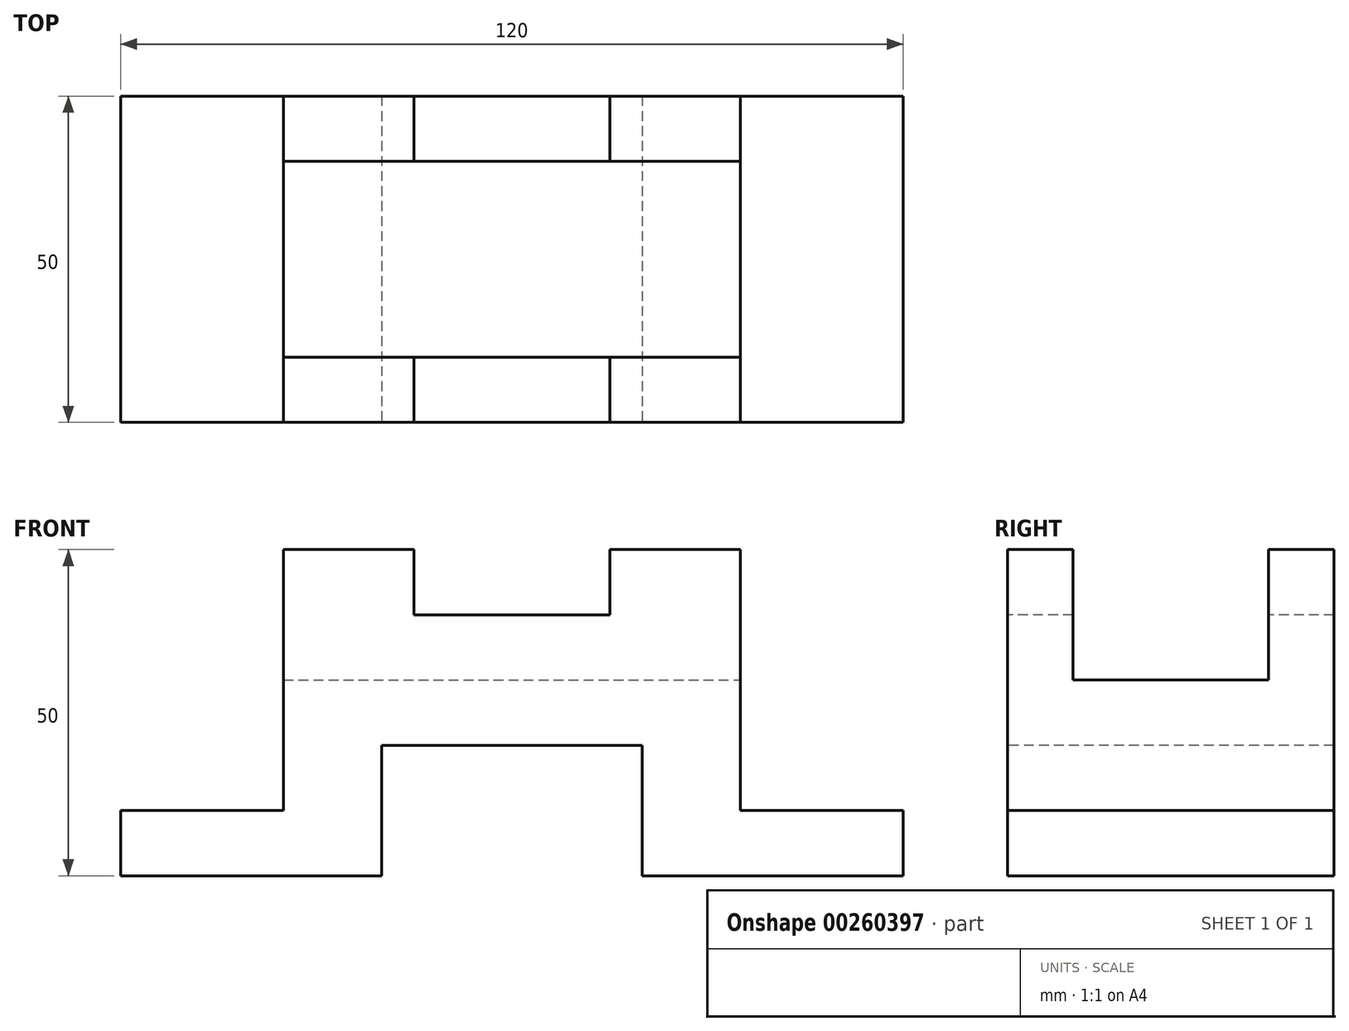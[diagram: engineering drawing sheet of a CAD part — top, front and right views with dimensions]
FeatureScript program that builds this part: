
annotation { "Feature Type Name" : "Feature", "Feature Type Description" : "" }
export const myFeature = defineFeature(function(context is Context, id is Id, definition is map)
    precondition{}
    {
        {
            assignVariable(context, id + "F0", {"name" : "B", "anyValue" : 50});
        }
        {
            var Q0;
            Q0=qCreatedBy(makeId("Top.planeOp"),FACE);
            var sketch = newSketch(context, id + "F1", { "sketchPlane" : qUnion([Q0])});
            skLineSegment(sketch, "E0.bottom", {"start": v(60, 25) * mm, "end": v(-60, 25) * mm});
            skLineSegment(sketch, "E0.top", {"start": v(60, -25) * mm, "end": v(-60, -25) * mm});
            skLineSegment(sketch, "E0.left", {"start": v(60, 25) * mm, "end": v(60, -25) * mm});
            skLineSegment(sketch, "E0.right", {"start": v(-60, 25) * mm, "end": v(-60, -25) * mm});
            skPoint(sketch, "E0.middle", {"position": v(0, 0) * mm});
            skSolve(sketch);
        }
        {
            var Q0;
            Q0 = qSketchRegion(id + "F1", true);
            extrude(context, id + "F2", {"entities" : qUnion([Q0]), "depth" : (getVariable(context, 'B')) * mm});
        }
        {
            var Q0;
            Q0=makeQuery(id+"F2.opExtrude","SWEPT_FACE",FACE,{"disambiguationData":[OSD([sQuery(id+"F1.wireOp",EDGE,"E0.top")])]});
            var sketch = newSketch(context, id + "F3", { "sketchPlane" : qUnion([Q0])});
            skLineSegment(sketch, "E1.bottom", {"start": v(-20, 20) * mm, "end": v(20, 20) * mm});
            skLineSegment(sketch, "E1.top", {"start": v(-20, -20) * mm, "end": v(20, -20) * mm});
            skLineSegment(sketch, "E1.left", {"start": v(-20, 20) * mm, "end": v(-20, -20) * mm});
            skLineSegment(sketch, "E1.right", {"start": v(20, 20) * mm, "end": v(20, -20) * mm});
            skPoint(sketch, "E1.middle", {"position": v(0, 0) * mm});
            skLineSegment(sketch, "E2.bottom", {"start": v(15, 40) * mm, "end": v(-15, 40) * mm});
            skLineSegment(sketch, "E2.top", {"start": v(15, 60) * mm, "end": v(-15, 60) * mm});
            skLineSegment(sketch, "E2.left", {"start": v(15, 40) * mm, "end": v(15, 60) * mm});
            skLineSegment(sketch, "E2.right", {"start": v(-15, 40) * mm, "end": v(-15, 60) * mm});
            skPoint(sketch, "E2.middle", {"position": v(0, 50) * mm});
            skLineSegment(sketch, "E3.bottom", {"start": v(-60, 50) * mm, "end": v(-35, 50) * mm});
            skLineSegment(sketch, "E3.top", {"start": v(-60, 10) * mm, "end": v(-35, 10) * mm});
            skLineSegment(sketch, "E3.left", {"start": v(-60, 50) * mm, "end": v(-60, 10) * mm});
            skLineSegment(sketch, "E3.right", {"start": v(-35, 50) * mm, "end": v(-35, 10) * mm});
            skLineSegment(sketch, "E4.bottom", {"start": v(60, 50) * mm, "end": v(35, 50) * mm});
            skLineSegment(sketch, "E4.top", {"start": v(60, 10) * mm, "end": v(35, 10) * mm});
            skLineSegment(sketch, "E4.left", {"start": v(60, 50) * mm, "end": v(60, 10) * mm});
            skLineSegment(sketch, "E4.right", {"start": v(35, 50) * mm, "end": v(35, 10) * mm});
            skSolve(sketch);
        }
        {
            var Q0;
            Q0 = qSketchRegion(id + "F3", true);
            extrude(context, id + "F4", {"entities" : qUnion([Q0]), "operationType" : NewBodyOperationType.REMOVE, "oppositeDirection" : true, "depth" : 50 * mm});
        }
        {
            var Q0;
            Q0=makeQuery(id+"F4.boolean.opBoolean","COPY",FACE,{"derivedFrom":makeQuery(id+"F4.opExtrude","SWEPT_FACE",FACE,{"disambiguationData":[OSD([sQuery(id+"F3.wireOp",EDGE,"E4.right")])]})});
            var sketch = newSketch(context, id + "F5", { "sketchPlane" : qUnion([Q0])});
            skLineSegment(sketch, "E5.bottom", {"start": v(-15, 70) * mm, "end": v(15, 70) * mm});
            skLineSegment(sketch, "E5.top", {"start": v(-15, 30) * mm, "end": v(15, 30) * mm});
            skLineSegment(sketch, "E5.left", {"start": v(-15, 70) * mm, "end": v(-15, 30) * mm});
            skLineSegment(sketch, "E5.right", {"start": v(15, 70) * mm, "end": v(15, 30) * mm});
            skPoint(sketch, "E5.middle", {"position": v(0, 50) * mm});
            skSolve(sketch);
        }
        {
            var Q0;
            Q0 = qSketchRegion(id + "F5", true);
            extrude(context, id + "F6", {"entities" : qUnion([Q0]), "operationType" : NewBodyOperationType.REMOVE, "oppositeDirection" : true, "depth" : 70 * mm});
        }
    });
